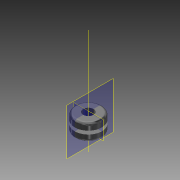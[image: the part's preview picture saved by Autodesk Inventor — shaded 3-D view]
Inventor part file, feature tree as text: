
AUTODESK INVENTOR PART (.ipt)
format: ipt  version: 2018 (Build 220112000, 112)  size: 134,144 bytes
history: native  units: in
note: dims shown in document units (in); Inventor stores cm internally (conversion verified against a paired STEP export)
features: plane x2, revolve x1, sketch x1, other x1
ambient origin geometry x8: Origin, YZ Plane, XZ Plane, XY Plane, X Axis, Y Axis, Z Axis, Center Point
bodies: Solid1 (feature_tree)
feature tree (5):
  plane  "Work Plane2"
  revolve  "Revolution1"  Angle=90.0deg
  plane  "Work Plane3"
  sketch  "Sketch2"  dims[d0=0.05in d1=90.0deg d2=0.05in d4=0.1562in d5=0.3125in d6=90.0deg]
  other  "Work Axis2"
